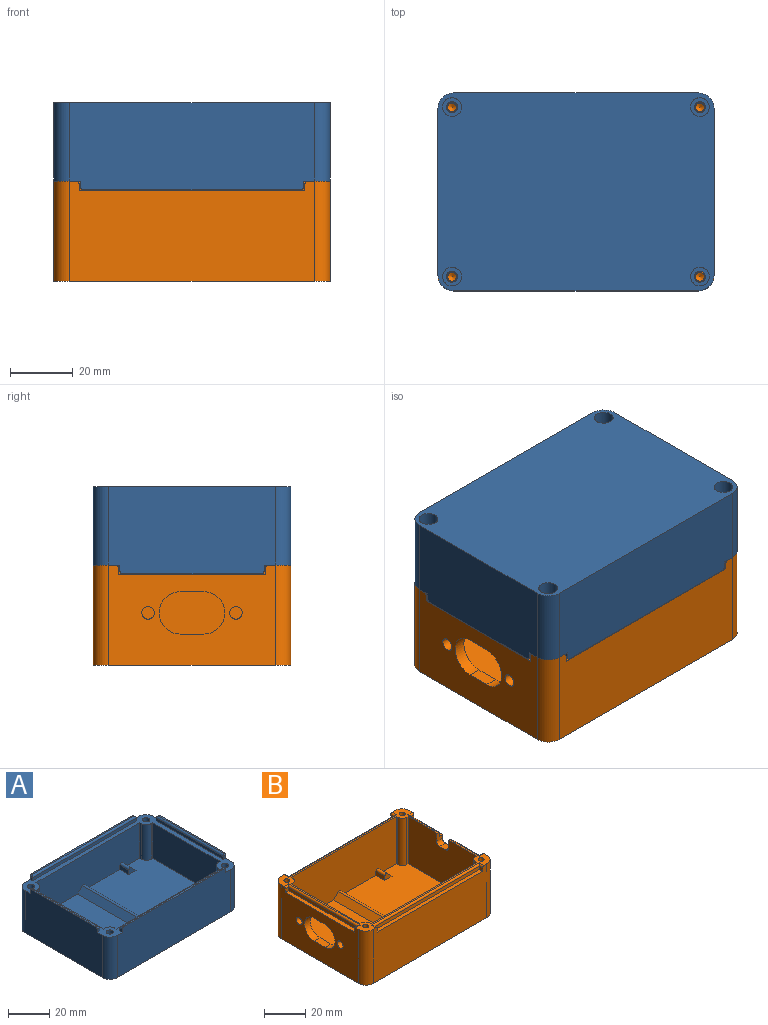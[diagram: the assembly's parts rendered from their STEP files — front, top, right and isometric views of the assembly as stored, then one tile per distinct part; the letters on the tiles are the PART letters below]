
ASSEMBLY  parts=2 mates=1
PART A: 79 faces, bbox 88x63x27.8 mm
  f0: plane 78x27.8mm, normal (0,1,0), area 2148.4mm2, adj f10,f14,f23,f37,f39,f62,f63,f73
  f1: plane 78x27.8mm, normal (0,-1,0), area 2148.4mm2, adj f7,f14,f23,f42,f43,f60,f61,f64
  f2: plane 53x27.8mm, normal (-1,0,0), area 1453.4mm2, adj f8,f14,f23,f38,f44,f60,f63,f67
  f3: plane 71x1.8mm, normal (0,1,0), area 127.8mm2, adj f14,f42,f43,f65
  f4: plane 46x1.8mm, normal (1,0,0), area 82.8mm2, adj f14,f38,f44,f68
  f5: plane 71x1.8mm, normal (0,-1,0), area 127.8mm2, adj f14,f37,f39,f74
  f6: plane 46x1.8mm, normal (-1,0,0), area 82.8mm2, adj f14,f40,f41,f71
  f7: plane 69x0.8mm, normal (0,0,1), area 55.2mm2, adj f1,f64,f65,f66
  f8: plane 44x0.8mm, normal (0,0,1), area 35.2mm2, adj f2,f67,f68,f69
  f9: plane 44x0.8mm, normal (0,0,1), area 35.2mm2, adj f24,f70,f71,f72
  f10: plane 69x0.8mm, normal (0,0,1), area 55.2mm2, adj f0,f73,f74,f75
  f11: plane 71x21mm, normal (0,-1,0), area 1468.5mm2, adj f13,f14,f15,f18,f19,f25,f28,f58
  f12: plane 46x21mm, normal (1,0,0), area 966mm2, adj f13,f14,f26,f36
  f13: plane 55x33mm, normal (0,0,1), area 1779.8mm2, adj f11,f12,f16,f25,f26,f27,f34,f35
  f14: plane 88x63mm, normal (0,0,1), area 733.3mm2, adj f0,f1,f2,f3,f4,f5,f6,f11
  f15: plane 55x42mm, normal (0,0,1), area 2214.8mm2, adj f11,f16,f17,f18,f19,f20,f21,f22
  f16: plane 71x21mm, normal (0,1,0), area 1468.5mm2, adj f13,f14,f15,f18,f22,f33,f34,f57
  f17: plane 46x21mm, normal (-1,0,0), area 966mm2, adj f14,f15,f30,f31
  f18: plane 55x2.59mm, normal (1,0,0), area 142.2mm2, adj f11,f15,f16,f78
  f19: plane 6x2.59mm, normal (-1,0,0), area 15.5mm2, adj f11,f15,f20,f77
  f20: plane 5x3.59mm, normal (0,-1,0), area 11.3mm2, adj f15,f19,f58,f77
  f21: plane 5x3.59mm, normal (0,1,0), area 11.3mm2, adj f15,f22,f57,f76
  f22: plane 6x2.59mm, normal (-1,0,0), area 15.5mm2, adj f15,f16,f21,f76
  f23: plane 88x63mm, normal (0,0,-1), area 5409.4mm2, adj f0,f1,f2,f24,f47,f50,f53,f56
  f24: plane 53x27.8mm, normal (1,0,0), area 1453.4mm2, adj f9,f14,f23,f40,f41,f61,f62,f70
  f25: plane 21x1mm, normal (1,0,0), area 21mm2, adj f11,f13,f14,f27
  f26: plane 21x1mm, normal (0,-1,0), area 21mm2, adj f12,f13,f14,f27
  f27: cylinder r=3.5mm len=21mm, axis (0,0,1), area 115.5mm2, adj f13,f14,f25,f26
  f28: plane 21x1mm, normal (-1,0,0), area 21mm2, adj f11,f14,f15,f29
  f29: cylinder r=3.5mm len=21mm, axis (0,0,1), area 115.5mm2, adj f14,f15,f28,f30
  f30: plane 21x1mm, normal (0,-1,0), area 21mm2, adj f14,f15,f17,f29
  f31: plane 21x1mm, normal (0,1,0), area 21mm2, adj f14,f15,f17,f32
  f32: cylinder r=3.5mm len=21mm, axis (0,0,1), area 115.5mm2, adj f14,f15,f31,f33
  f33: plane 21x1mm, normal (-1,0,0), area 21mm2, adj f14,f15,f16,f32
  f34: plane 21x1mm, normal (1,0,0), area 21mm2, adj f13,f14,f16,f35
  f35: cylinder r=3.5mm len=21mm, axis (0,0,1), area 115.5mm2, adj f13,f14,f34,f36
  f36: plane 21x1mm, normal (0,1,0), area 21mm2, adj f12,f13,f14,f35
  f37: plane 1.8x1.8mm, normal (-1,0,0), area 3.2mm2, adj f0,f5,f14,f73
  f38: plane 1.8x1.8mm, normal (0,1,0), area 3.2mm2, adj f2,f4,f14,f67
  f39: plane 1.8x1.8mm, normal (1,0,0), area 3.2mm2, adj f0,f5,f14,f75
  f40: plane 1.8x1.8mm, normal (0,1,0), area 3.2mm2, adj f6,f14,f24,f70
  f41: plane 1.8x1.8mm, normal (0,-1,0), area 3.2mm2, adj f6,f14,f24,f72
  f42: plane 1.8x1.8mm, normal (1,0,0), area 3.2mm2, adj f1,f3,f14,f64
  f43: plane 1.8x1.8mm, normal (-1,0,0), area 3.2mm2, adj f1,f3,f14,f66
  f44: plane 1.8x1.8mm, normal (0,-1,0), area 3.2mm2, adj f2,f4,f14,f69
  f45: cylinder r=1.75mm len=5mm, axis (0,0,-1), area 55mm2, adj f14,f46
  f46: plane 6x6mm, normal (0,0,-1), area 18.7mm2, adj f45,f47
  f47: cylinder r=3mm len=20mm, axis (0,0,-1), area 377mm2, adj f23,f46
  f48: cylinder r=1.75mm len=5mm, axis (0,0,-1), area 55mm2, adj f14,f49
  f49: plane 6x6mm, normal (0,0,-1), area 18.7mm2, adj f48,f50
  f50: cylinder r=3mm len=20mm, axis (0,0,-1), area 377mm2, adj f23,f49
  f51: cylinder r=1.75mm len=5mm, axis (0,0,-1), area 55mm2, adj f14,f52
  f52: plane 6x6mm, normal (0,0,-1), area 18.7mm2, adj f51,f53
  f53: cylinder r=3mm len=20mm, axis (0,0,-1), area 377mm2, adj f23,f52
  f54: cylinder r=1.75mm len=5mm, axis (0,0,-1), area 55mm2, adj f14,f55
  f55: plane 6x6mm, normal (0,0,-1), area 18.7mm2, adj f54,f56
  f56: cylinder r=3mm len=20mm, axis (0,0,-1), area 377mm2, adj f23,f55
  f57: plane 6x3.29mm, normal (0.71,0,0.71), area 27.9mm2, adj f15,f16,f21,f76
  f58: plane 6x3.29mm, normal (0.71,0,0.71), area 27.9mm2, adj f11,f15,f20,f77
  f59: plane 55x3.29mm, normal (-0.71,0,0.71), area 256.1mm2, adj f11,f13,f16,f78
  f60: cylinder r=5mm len=25mm, axis (0,0,-1), area 196.3mm2, adj f1,f2,f14,f23
  f61: cylinder r=5mm len=25mm, axis (0,0,1), area 196.3mm2, adj f1,f14,f23,f24
  f62: cylinder r=5mm len=25mm, axis (0,0,-1), area 196.3mm2, adj f0,f14,f23,f24
  f63: cylinder r=5mm len=25mm, axis (0,0,1), area 196.3mm2, adj f0,f2,f14,f23
  f64: cylinder r=1mm len=1.8mm, axis (0,1,0), area 2.3mm2, adj f1,f7,f42,f65
  f65: cylinder r=1mm len=71mm, axis (1,0,0), area 110.4mm2, adj f3,f7,f64,f66
  f66: cylinder r=1mm len=1.8mm, axis (0,-1,0), area 2.3mm2, adj f1,f7,f43,f65
  f67: cylinder r=1mm len=1.8mm, axis (-1,0,0), area 2.3mm2, adj f2,f8,f38,f68
  f68: cylinder r=1mm len=46mm, axis (0,-1,0), area 71.1mm2, adj f4,f8,f67,f69
  f69: cylinder r=1mm len=1.8mm, axis (1,0,0), area 2.3mm2, adj f2,f8,f44,f68
  f70: cylinder r=1mm len=1.8mm, axis (-1,0,0), area 2.3mm2, adj f9,f24,f40,f71
  f71: cylinder r=1mm len=46mm, axis (0,1,0), area 71.1mm2, adj f6,f9,f70,f72
  f72: cylinder r=1mm len=1.8mm, axis (1,0,0), area 2.3mm2, adj f9,f24,f41,f71
  f73: cylinder r=1mm len=1.8mm, axis (0,-1,0), area 2.3mm2, adj f0,f10,f37,f74
  f74: cylinder r=1mm len=71mm, axis (-1,0,0), area 110.4mm2, adj f5,f10,f73,f75
  f75: cylinder r=1mm len=1.8mm, axis (0,1,0), area 2.3mm2, adj f0,f10,f39,f74
  f76: cylinder r=1mm len=6mm, axis (0,-1,0), area 14.1mm2, adj f16,f21,f22,f57
  f77: cylinder r=1mm len=6mm, axis (0,-1,0), area 14.1mm2, adj f11,f19,f20,f58
  f78: cylinder r=1mm len=55mm, axis (0,-1,0), area 129.6mm2, adj f11,f16,f18,f59
PART B: 90 faces, bbox 88x63x32 mm
  f0: plane 47x28mm, normal (-1,0,0), area 1261.3mm2, adj f3,f17,f31,f33,f54,f55,f56,f70
  f1: plane 19.5x2mm, normal (1,0,0), area 39mm2, adj f2,f41,f54,f76
  f2: plane 19.5x2.2mm, normal (0,0,1), area 42.9mm2, adj f1,f4,f41,f54
  f3: plane 88x63mm, normal (0,0,1), area 357.3mm2, adj f0,f4,f5,f8,f13,f24,f25,f26
  f4: plane 53x32mm, normal (1,0,0), area 1524.3mm2, adj f2,f3,f11,f23,f41,f43,f54,f55
  f5: plane 72x28mm, normal (0,1,0), area 1993.5mm2, adj f3,f16,f17,f18,f22,f35,f36,f63
  f6: plane 72x2mm, normal (0,-1,0), area 144mm2, adj f7,f42,f44,f82
  f7: plane 72x2.2mm, normal (0,0,1), area 158.4mm2, adj f6,f25,f42,f44
  f8: plane 47x28mm, normal (1,0,0), area 1046.5mm2, adj f3,f16,f28,f37,f57,f58,f59,f60
  f9: plane 47x2mm, normal (-1,0,0), area 94mm2, adj f15,f38,f45,f79
  f10: plane 19.5x2mm, normal (1,0,0), area 39mm2, adj f11,f43,f55,f74
  f11: plane 19.5x2.2mm, normal (0,0,1), area 42.9mm2, adj f4,f10,f43,f55
  f12: plane 72x2.2mm, normal (0,0,1), area 158.4mm2, adj f14,f24,f39,f40
  f13: plane 72x28mm, normal (0,-1,0), area 1993.5mm2, adj f3,f16,f17,f18,f19,f27,f30,f64
  f14: plane 72x2mm, normal (0,1,0), area 144mm2, adj f12,f39,f40,f85
  f15: plane 47x2.2mm, normal (0,0,1), area 103.4mm2, adj f9,f26,f38,f45
  f16: plane 55x33mm, normal (0,0,1), area 1788.2mm2, adj f5,f8,f13,f27,f28,f29,f36,f37
  f17: plane 55x42mm, normal (0,0,1), area 2221.9mm2, adj f0,f5,f13,f18,f19,f20,f21,f22
  f18: plane 55x2.59mm, normal (1,0,0), area 142.2mm2, adj f5,f13,f17,f89
  f19: plane 6x2.59mm, normal (-1,0,0), area 15.5mm2, adj f13,f17,f20,f88
  f20: plane 5x3.59mm, normal (0,-1,0), area 11.3mm2, adj f17,f19,f64,f88
  f21: plane 5x3.59mm, normal (0,1,0), area 11.3mm2, adj f17,f22,f63,f87
  f22: plane 6x2.59mm, normal (-1,0,0), area 15.5mm2, adj f5,f17,f21,f87
  f23: plane 88x63mm, normal (0,0,-1), area 5522.5mm2, adj f4,f24,f25,f26,f66,f67,f68,f69
  f24: plane 78x32mm, normal (0,1,0), area 2279.6mm2, adj f3,f12,f23,f39,f40,f68,f69,f84
  f25: plane 78x32mm, normal (0,-1,0), area 2279.6mm2, adj f3,f7,f23,f42,f44,f66,f67,f81
  f26: plane 53x32mm, normal (-1,0,0), area 1285mm2, adj f3,f15,f23,f38,f45,f57,f58,f59
  f27: plane 28x1mm, normal (1,0,0), area 28mm2, adj f3,f13,f16,f29
  f28: plane 28x1mm, normal (0,-1,0), area 28mm2, adj f3,f8,f16,f29
  f29: cylinder r=3mm len=28mm, axis (0,0,1), area 131.9mm2, adj f3,f16,f27,f28
  f30: plane 28x1mm, normal (-1,0,0), area 28mm2, adj f3,f13,f17,f32
  f31: plane 28x1mm, normal (0,-1,0), area 28mm2, adj f0,f3,f17,f32
  f32: cylinder r=3mm len=28mm, axis (0,0,1), area 131.9mm2, adj f3,f17,f30,f31
  f33: plane 28x1mm, normal (0,1,0), area 28mm2, adj f0,f3,f17,f34
  f34: cylinder r=3mm len=28mm, axis (0,0,1), area 131.9mm2, adj f3,f17,f33,f35
  f35: plane 28x1mm, normal (-1,0,0), area 28mm2, adj f3,f5,f17,f34
  f36: cylinder r=4.1mm len=28mm, axis (0,0,1), area 154.6mm2, adj f3,f5,f16,f37
  f37: plane 28x0.81mm, normal (0,1,0), area 22.8mm2, adj f3,f8,f16,f36
  f38: plane 2.2x2mm, normal (0,-1,0), area 4.4mm2, adj f9,f15,f26,f78
  f39: plane 2.2x2mm, normal (1,0,0), area 4.4mm2, adj f12,f14,f24,f84
  f40: plane 2.2x2mm, normal (-1,0,0), area 4.4mm2, adj f12,f14,f24,f86
  f41: plane 2.2x2mm, normal (0,-1,0), area 4.4mm2, adj f1,f2,f4,f75
  f42: plane 2.2x2mm, normal (-1,0,0), area 4.4mm2, adj f6,f7,f25,f83
  f43: plane 2.2x2mm, normal (0,1,0), area 4.4mm2, adj f4,f10,f11,f73
  f44: plane 2.2x2mm, normal (1,0,0), area 4.4mm2, adj f6,f7,f25,f81
  f45: plane 2.2x2mm, normal (0,1,0), area 4.4mm2, adj f9,f15,f26,f80
  f46: cylinder r=1.41mm len=28mm, axis (0,0,1), area 248.1mm2, adj f3,f47
  f47: cone r=0mm half-angle=59deg, axis (0,0,1), area 7.3mm2, adj f46
  f48: cylinder r=1.41mm len=28mm, axis (0,0,1), area 248.1mm2, adj f3,f49
  f49: cone r=0mm half-angle=59deg, axis (0,0,1), area 7.3mm2, adj f48
  f50: cylinder r=1.41mm len=28mm, axis (0,0,1), area 248.1mm2, adj f3,f51
  f51: cone r=0mm half-angle=59deg, axis (0,0,1), area 7.3mm2, adj f50
  f52: cylinder r=1.41mm len=28mm, axis (0,0,1), area 248.1mm2, adj f3,f53
  f53: cone r=0mm half-angle=59deg, axis (0,0,1), area 7.3mm2, adj f52
  f54: plane 4x4mm, normal (0,-1,0), area 11.6mm2, adj f0,f1,f2,f4,f71,f77
  f55: plane 4x4mm, normal (0,1,0), area 11.6mm2, adj f0,f4,f10,f11,f70,f72
  f56: plane 4x4mm, normal (0,0,1), area 16mm2, adj f0,f4,f70,f71
  f57: plane 7.5x4mm, normal (0,0,1), area 30mm2, adj f8,f26,f58,f60
  f58: cylinder r=6.75mm len=13.5mm, axis (-1,0,0), area 84.8mm2, adj f8,f26,f57,f59
  f59: plane 7.5x4mm, normal (0,0,-1), area 30mm2, adj f8,f26,f58,f60
  f60: cylinder r=6.75mm len=13.5mm, axis (-1,0,0), area 84.8mm2, adj f8,f26,f57,f59
  f61: cylinder r=2mm len=4mm, axis (-1,0,0), area 50.3mm2, adj f8,f26
  f62: cylinder r=2mm len=4mm, axis (-1,0,0), area 50.3mm2, adj f8,f26
  f63: plane 6x3.29mm, normal (0.71,0,0.71), area 27.9mm2, adj f5,f17,f21,f87
  f64: plane 6x3.29mm, normal (0.71,0,0.71), area 27.9mm2, adj f13,f17,f20,f88
  f65: plane 55x3.29mm, normal (-0.71,0,0.71), area 256.1mm2, adj f5,f13,f16,f89
  f66: cylinder r=5mm len=32mm, axis (0,0,-1), area 251.3mm2, adj f3,f23,f25,f26
  f67: cylinder r=5mm len=32mm, axis (0,0,1), area 251.3mm2, adj f3,f4,f23,f25
  f68: cylinder r=5mm len=32mm, axis (0,0,-1), area 251.3mm2, adj f3,f4,f23,f24
  f69: cylinder r=5mm len=32mm, axis (0,0,1), area 251.3mm2, adj f3,f23,f24,f26
  f70: cylinder r=2mm len=4mm, axis (-1,0,0), area 12.6mm2, adj f0,f4,f55,f56
  f71: cylinder r=2mm len=4mm, axis (1,0,0), area 12.6mm2, adj f0,f4,f54,f56
  f72: cylinder r=1mm len=1.8mm, axis (-1,0,0), area 2.3mm2, adj f0,f3,f55,f74
  f73: cylinder r=1mm len=3.2mm, axis (1,0,0), area 4mm2, adj f3,f4,f43,f74
  f74: cylinder r=1mm len=20.5mm, axis (0,-1,0), area 30.6mm2, adj f3,f10,f72,f73
  f75: cylinder r=1mm len=3.2mm, axis (-1,0,0), area 4mm2, adj f3,f4,f41,f76
  f76: cylinder r=1mm len=20.5mm, axis (0,-1,0), area 30.6mm2, adj f1,f3,f75,f77
  f77: cylinder r=1mm len=1.8mm, axis (1,0,0), area 2.3mm2, adj f0,f3,f54,f76
  f78: cylinder r=1mm len=3.2mm, axis (-1,0,0), area 4mm2, adj f3,f26,f38,f79
  f79: cylinder r=1mm len=49mm, axis (0,1,0), area 75mm2, adj f3,f9,f78,f80
  f80: cylinder r=1mm len=3.2mm, axis (1,0,0), area 4mm2, adj f3,f26,f45,f79
  f81: cylinder r=1mm len=3.2mm, axis (0,-1,0), area 4mm2, adj f3,f25,f44,f82
  f82: cylinder r=1mm len=74mm, axis (-1,0,0), area 114.2mm2, adj f3,f6,f81,f83
  f83: cylinder r=1mm len=3.2mm, axis (0,1,0), area 4mm2, adj f3,f25,f42,f82
  f84: cylinder r=1mm len=3.2mm, axis (0,-1,0), area 4mm2, adj f3,f24,f39,f85
  f85: cylinder r=1mm len=74mm, axis (1,0,0), area 114.2mm2, adj f3,f14,f84,f86
  f86: cylinder r=1mm len=3.2mm, axis (0,1,0), area 4mm2, adj f3,f24,f40,f85
  f87: cylinder r=1mm len=6mm, axis (0,-1,0), area 14.1mm2, adj f5,f21,f22,f63
  f88: cylinder r=1mm len=6mm, axis (0,-1,0), area 14.1mm2, adj f13,f19,f20,f64
  f89: cylinder r=1mm len=55mm, axis (0,-1,0), area 129.6mm2, adj f5,f13,f18,f65
PLACE A rot(axis=(1,0,0),180deg) t=(-0.5,-54.5,52)mm
PLACE B t=(-0.5,0.5,3)mm
MATE parallel A.f48 <-> B.f50  axis (0,0,-1) through (-1,-54,31)mm
